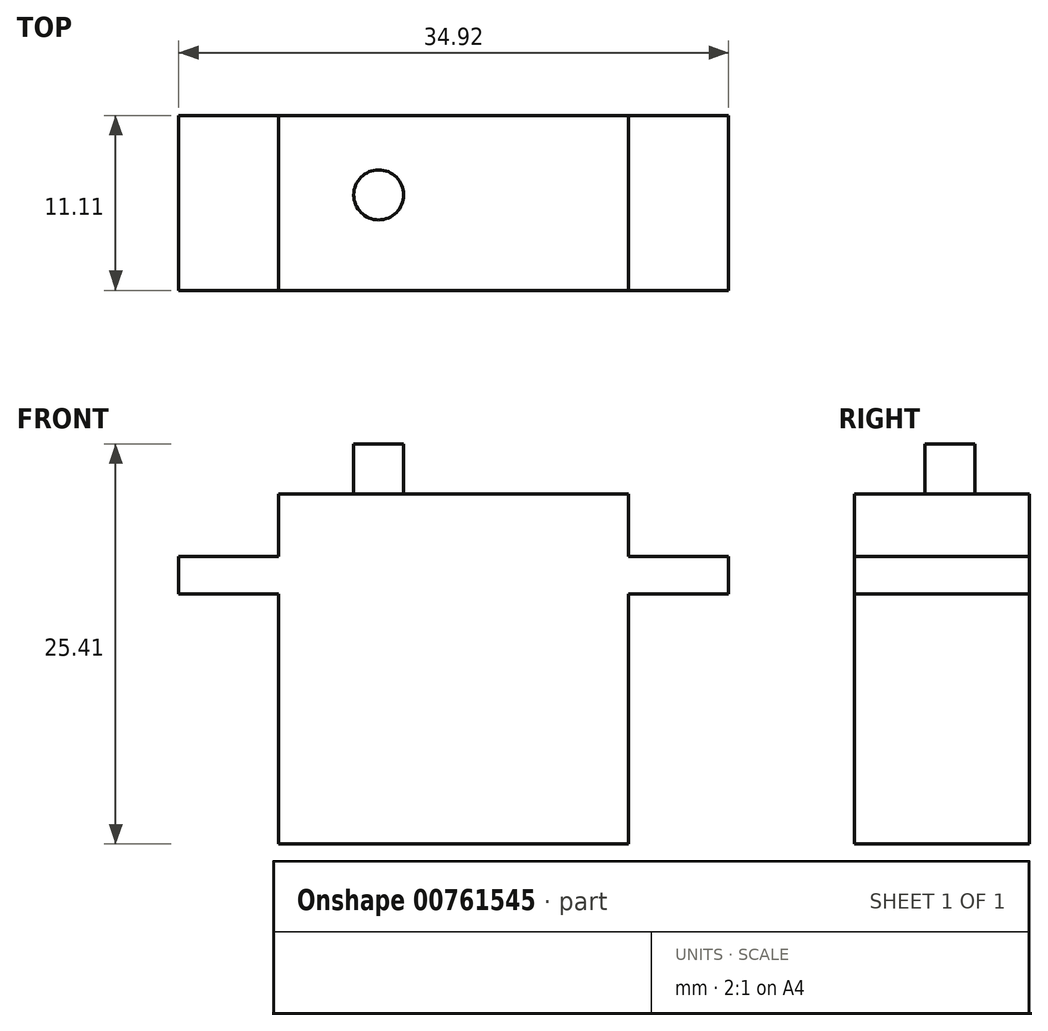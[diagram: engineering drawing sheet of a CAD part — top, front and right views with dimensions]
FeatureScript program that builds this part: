
annotation { "Feature Type Name" : "Feature", "Feature Type Description" : "" }
export const myFeature = defineFeature(function(context is Context, id is Id, definition is map)
    precondition{}
    {
        {
            var Q0;
            Q0=qCreatedBy(makeId("Front.planeOp"),FACE);
            var sketch = newSketch(context, id + "F0", { "sketchPlane" : qUnion([Q0])});
            skLineSegment(sketch, "E0.bottom", {"start": v(0, 0) * mm, "end": v(22.23, 0) * mm});
            skLineSegment(sketch, "E0.top", {"start": v(0, -22.23) * mm, "end": v(22.23, -22.23) * mm});
            skLineSegment(sketch, "E0.left", {"start": v(0, 0) * mm, "end": v(0, -22.23) * mm});
            skLineSegment(sketch, "E0.right", {"start": v(22.23, 0) * mm, "end": v(22.23, -22.23) * mm});
            skSolve(sketch);
        }
        {
            var Q0;
            Q0 = qSketchRegion(id + "F0", true);
            extrude(context, id + "F1", {"entities" : qUnion([Q0]), "depth" : 11.1 * mm, "offsetDistance" : 25.4 * mm});
        }
        {
            var Q0;
            Q0=makeQuery(id+"F1.opExtrude","SWEPT_FACE",FACE,{"disambiguationData":[OSD([sQuery(id+"F0.wireOp",EDGE,"E0.right")])]});
            var sketch = newSketch(context, id + "F2", { "sketchPlane" : qUnion([Q0])});
            skLineSegment(sketch, "E1", {"start": v(-11.11, -3.97) * mm, "end": v(-11.11, -6.35) * mm});
            skLineSegment(sketch, "E2", {"start": v(-11.11, -6.35) * mm, "end": v(0, -6.35) * mm});
            skLineSegment(sketch, "E3", {"start": v(0, -6.35) * mm, "end": v(0, -3.97) * mm});
            skLineSegment(sketch, "E4", {"start": v(0, -3.97) * mm, "end": v(-11.11, -3.97) * mm});
            skSolve(sketch);
        }
        {
            var Q0;
            Q0=makeQuery(id+"F2.imprint","IMPRINT",FACE,{"disambiguationData":[TD([[makeQuery(id+"F2.imprint","IMPRINT",EDGE,{"derivedFrom":sQuery(id+"F2.wireOp",EDGE,"E1")}),1.0]])]});
            extrude(context, id + "F3", {"entities" : qUnion([Q0]), "operationType" : NewBodyOperationType.ADD, "depth" : 6.35 * mm, "offsetDistance" : 25.4 * mm});
        }
        {
            var Q0;
            Q0=makeQuery(id+"F1.opExtrude","SWEPT_FACE",FACE,{"disambiguationData":[OSD([sQuery(id+"F0.wireOp",EDGE,"E0.left")])]});
            var sketch = newSketch(context, id + "F4", { "sketchPlane" : qUnion([Q0])});
            skLineSegment(sketch, "E5.bottom", {"start": v(0, -3.97) * mm, "end": v(11.11, -3.97) * mm});
            skLineSegment(sketch, "E5.top", {"start": v(0, -6.35) * mm, "end": v(11.11, -6.35) * mm});
            skLineSegment(sketch, "E5.left", {"start": v(0, -3.97) * mm, "end": v(0, -6.35) * mm});
            skLineSegment(sketch, "E5.right", {"start": v(11.11, -3.97) * mm, "end": v(11.11, -6.35) * mm});
            skSolve(sketch);
        }
        {
            var Q0;
            Q0 = qSketchRegion(id + "F4", true);
            extrude(context, id + "F5", {"entities" : qUnion([Q0]), "operationType" : NewBodyOperationType.ADD, "depth" : 6.35 * mm, "offsetDistance" : 25.4 * mm});
        }
        {
            var Q0;
            Q0=makeQuery(id+"F1.opExtrude","SWEPT_FACE",FACE,{"disambiguationData":[OSD([sQuery(id+"F0.wireOp",EDGE,"E0.bottom")])]});
            var sketch = newSketch(context, id + "F6", { "sketchPlane" : qUnion([Q0])});
            skCircle(sketch, "E6", {"center": v(6.35, -5.04) * mm, "radius": 1.59 * mm});
            skSolve(sketch);
        }
        {
            var Q0;
            Q0=makeQuery(id+"F6.imprint","IMPRINT",FACE,{"disambiguationData":[TD([[makeQuery(id+"F6.imprint","IMPRINT",EDGE,{"derivedFrom":sQuery(id+"F6.wireOp",EDGE,"E6")}),1.0]])]});
            extrude(context, id + "F7", {"entities" : qUnion([Q0]), "operationType" : NewBodyOperationType.ADD, "depth" : 3.17 * mm, "offsetDistance" : 25.4 * mm});
        }
    });
